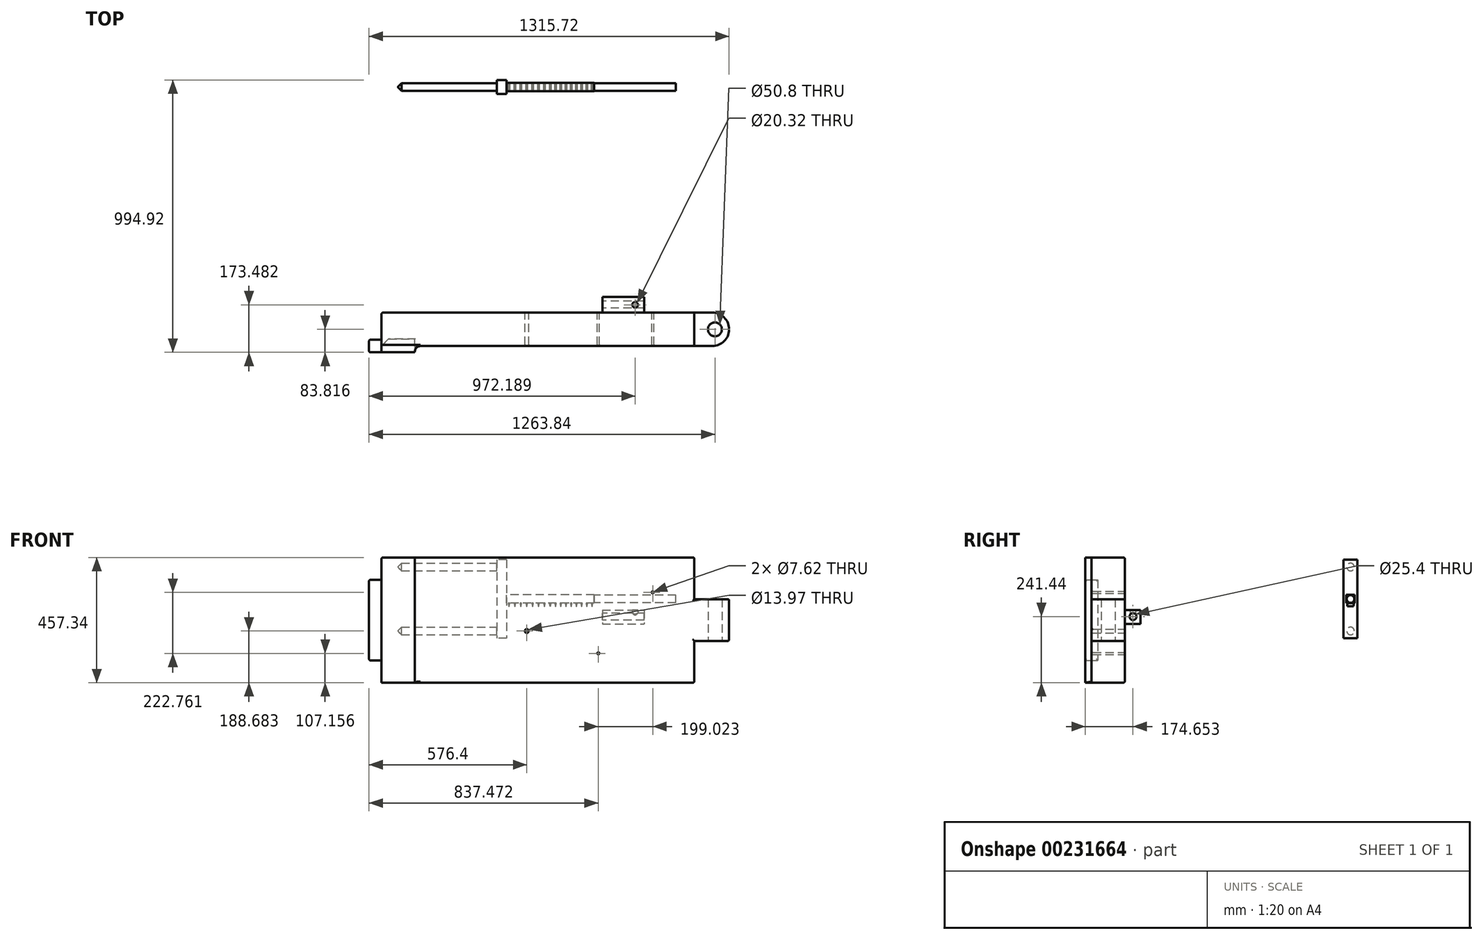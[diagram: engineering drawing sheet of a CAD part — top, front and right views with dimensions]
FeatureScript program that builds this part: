
annotation { "Feature Type Name" : "Feature", "Feature Type Description" : "" }
export const myFeature = defineFeature(function(context is Context, id is Id, definition is map)
    precondition{}
    {
        {
            var Q0;
            Q0=qCreatedBy(makeId("Right.planeOp"),FACE);
            var sketch = newSketch(context, id + "F0", { "sketchPlane" : qUnion([Q0])});
            skLineSegment(sketch, "E0", {"start": v(0, 0) * mm, "end": v(0, 121.92) * mm, "construction": true});
            skLineSegment(sketch, "E1", {"start": v(0, 0) * mm, "end": v(0, -121.92) * mm, "construction": true});
            skCircle(sketch, "E2", {"center": v(0, 121.92) * mm, "radius": 15.24 * mm});
            skCircle(sketch, "E3", {"center": v(0, -121.92) * mm, "radius": 15.24 * mm});
            skLineSegment(sketch, "E4.bottom", {"start": v(25.4, 143.51) * mm, "end": v(-25.4, 143.51) * mm});
            skLineSegment(sketch, "E4.top", {"start": v(25.4, -143.51) * mm, "end": v(-25.4, -143.51) * mm});
            skLineSegment(sketch, "E4.left", {"start": v(25.4, 143.51) * mm, "end": v(25.4, -143.51) * mm});
            skLineSegment(sketch, "E4.right", {"start": v(-25.4, 143.51) * mm, "end": v(-25.4, -143.51) * mm});
            skPoint(sketch, "E4.middle", {"position": v(0, 0) * mm});
            skLineSegment(sketch, "E5.bottom", {"start": v(15.24, -15.24) * mm, "end": v(-15.24, -15.24) * mm});
            skLineSegment(sketch, "E5.top", {"start": v(15.24, 15.24) * mm, "end": v(-15.24, 15.24) * mm});
            skLineSegment(sketch, "E5.left", {"start": v(15.24, -15.24) * mm, "end": v(15.24, 15.24) * mm});
            skLineSegment(sketch, "E5.right", {"start": v(-15.24, -15.24) * mm, "end": v(-15.24, 15.24) * mm});
            skSolve(sketch);
        }
        {
            var Q0;
            Q0 = qSketchRegion(id + "F0", true);
            var Q1;
            Q1=makeQuery(id+"F0.imprint","IMPRINT",FACE,{"disambiguationData":[TD([[makeQuery(id+"F0.imprint","IMPRINT",EDGE,{"derivedFrom":sQuery(id+"F0.wireOp",EDGE,"E2")}),1.0]])]});
            var Q2;
            Q2=makeQuery(id+"F0.imprint","IMPRINT",FACE,{"disambiguationData":[TD([[makeQuery(id+"F0.imprint","IMPRINT",EDGE,{"derivedFrom":sQuery(id+"F0.wireOp",EDGE,"E3")}),1.0]])]});
            extrude(context, id + "F1", {"entities" : qUnion([Q0, Q1, Q2]), "depth" : 35.56 * mm});
        }
        {
            var Q0;
            Q0=qCreatedBy(makeId("Right.planeOp"),FACE);
            var sketch = newSketch(context, id + "F2", { "sketchPlane" : qUnion([Q0])});
            skLineSegment(sketch, "E6.bottom", {"start": v(15.24, 15.24) * mm, "end": v(-15.24, 15.24) * mm});
            skLineSegment(sketch, "E6.top", {"start": v(15.24, -15.24) * mm, "end": v(-15.24, -15.24) * mm});
            skLineSegment(sketch, "E6.left", {"start": v(15.24, 15.24) * mm, "end": v(15.24, -15.24) * mm});
            skLineSegment(sketch, "E6.right", {"start": v(-15.24, 15.24) * mm, "end": v(-15.24, -15.24) * mm});
            skPoint(sketch, "E6.middle", {"position": v(0, 0) * mm});
            skSolve(sketch);
        }
        {
            var Q0;
            Q0=makeQuery(id+"F2.imprint","IMPRINT",FACE,{"disambiguationData":[TD([[makeQuery(id+"F2.imprint","IMPRINT",EDGE,{"derivedFrom":sQuery(id+"F2.wireOp",EDGE,"E6.bottom")}),1.0]])]});
            extrude(context, id + "F3", {"entities" : qUnion([Q0]), "operationType" : NewBodyOperationType.ADD, "depth" : 355.6 * mm});
        }
        {
            var Q0;
            Q0=qCreatedBy(makeId("Top.planeOp"),FACE);
            var sketch = newSketch(context, id + "F4", { "sketchPlane" : qUnion([Q0])});
            skLineSegment(sketch, "E7", {"start": v(35.48, 0) * mm, "end": v(355.44, 0) * mm, "construction": true});
            skLineSegment(sketch, "E8.bottom", {"start": v(198.63, 12.7) * mm, "end": v(192.28, 12.7) * mm});
            skLineSegment(sketch, "E8.top", {"start": v(198.63, -12.7) * mm, "end": v(192.28, -12.7) * mm});
            skLineSegment(sketch, "E8.left", {"start": v(198.63, 12.7) * mm, "end": v(198.63, -12.7) * mm});
            skLineSegment(sketch, "E8.right", {"start": v(192.28, 12.7) * mm, "end": v(192.28, -12.7) * mm});
            skPoint(sketch, "E8.middle", {"position": v(195.46, 0) * mm});
            skLineSegment(sketch, "E9.1.0.0", {"start": v(217.68, 12.7) * mm, "end": v(217.68, -12.7) * mm});
            skLineSegment(sketch, "E9.1.0.1", {"start": v(211.33, 12.7) * mm, "end": v(211.33, -12.7) * mm});
            skLineSegment(sketch, "E9.1.0.2", {"start": v(217.68, -12.7) * mm, "end": v(211.33, -12.7) * mm});
            skLineSegment(sketch, "E9.1.0.3", {"start": v(217.68, 12.7) * mm, "end": v(211.33, 12.7) * mm});
            skLineSegment(sketch, "E9.2.0.0", {"start": v(236.73, 12.7) * mm, "end": v(236.73, -12.7) * mm});
            skLineSegment(sketch, "E9.2.0.1", {"start": v(230.38, 12.7) * mm, "end": v(230.38, -12.7) * mm});
            skLineSegment(sketch, "E9.2.0.2", {"start": v(236.73, -12.7) * mm, "end": v(230.38, -12.7) * mm});
            skLineSegment(sketch, "E9.2.0.3", {"start": v(236.73, 12.7) * mm, "end": v(230.38, 12.7) * mm});
            skLineSegment(sketch, "E9.3.0.0", {"start": v(255.78, 12.7) * mm, "end": v(255.78, -12.7) * mm});
            skLineSegment(sketch, "E9.3.0.1", {"start": v(249.43, 12.7) * mm, "end": v(249.43, -12.7) * mm});
            skLineSegment(sketch, "E9.3.0.2", {"start": v(255.78, -12.7) * mm, "end": v(249.43, -12.7) * mm});
            skLineSegment(sketch, "E9.3.0.3", {"start": v(255.78, 12.7) * mm, "end": v(249.43, 12.7) * mm});
            skLineSegment(sketch, "E9.4.0.0", {"start": v(274.83, 12.7) * mm, "end": v(274.83, -12.7) * mm});
            skLineSegment(sketch, "E9.4.0.1", {"start": v(268.48, 12.7) * mm, "end": v(268.48, -12.7) * mm});
            skLineSegment(sketch, "E9.4.0.2", {"start": v(274.83, -12.7) * mm, "end": v(268.48, -12.7) * mm});
            skLineSegment(sketch, "E9.4.0.3", {"start": v(274.83, 12.7) * mm, "end": v(268.48, 12.7) * mm});
            skLineSegment(sketch, "E9.5.0.0", {"start": v(293.88, 12.7) * mm, "end": v(293.88, -12.7) * mm});
            skLineSegment(sketch, "E9.5.0.1", {"start": v(287.53, 12.7) * mm, "end": v(287.53, -12.7) * mm});
            skLineSegment(sketch, "E9.5.0.2", {"start": v(293.88, -12.7) * mm, "end": v(287.53, -12.7) * mm});
            skLineSegment(sketch, "E9.5.0.3", {"start": v(293.88, 12.7) * mm, "end": v(287.53, 12.7) * mm});
            skLineSegment(sketch, "E9.6.0.0", {"start": v(312.93, 12.7) * mm, "end": v(312.93, -12.7) * mm});
            skLineSegment(sketch, "E9.6.0.1", {"start": v(306.58, 12.7) * mm, "end": v(306.58, -12.7) * mm});
            skLineSegment(sketch, "E9.6.0.2", {"start": v(312.93, -12.7) * mm, "end": v(306.58, -12.7) * mm});
            skLineSegment(sketch, "E9.6.0.3", {"start": v(312.93, 12.7) * mm, "end": v(306.58, 12.7) * mm});
            skLineSegment(sketch, "E9.7.0.0", {"start": v(331.98, 12.7) * mm, "end": v(331.98, -12.7) * mm});
            skLineSegment(sketch, "E9.7.0.1", {"start": v(325.63, 12.7) * mm, "end": v(325.63, -12.7) * mm});
            skLineSegment(sketch, "E9.7.0.2", {"start": v(331.98, -12.7) * mm, "end": v(325.63, -12.7) * mm});
            skLineSegment(sketch, "E9.7.0.3", {"start": v(331.98, 12.7) * mm, "end": v(325.63, 12.7) * mm});
            skLineSegment(sketch, "E9.8.0.0", {"start": v(351.03, 12.7) * mm, "end": v(351.03, -12.7) * mm});
            skLineSegment(sketch, "E9.8.0.1", {"start": v(344.68, 12.7) * mm, "end": v(344.68, -12.7) * mm});
            skLineSegment(sketch, "E9.8.0.2", {"start": v(351.03, -12.7) * mm, "end": v(344.68, -12.7) * mm});
            skLineSegment(sketch, "E9.8.0.3", {"start": v(351.03, 12.7) * mm, "end": v(344.68, 12.7) * mm});
            skLineSegment(sketch, "E9.direction1", {"start": v(198.63, -12.7) * mm, "end": v(217.68, -12.7) * mm, "construction": true});
            skLineSegment(sketch, "E10.1.0.0", {"start": v(177.04, -12.7) * mm, "end": v(170.7, -12.7) * mm});
            skLineSegment(sketch, "E10.1.0.1", {"start": v(170.7, 12.7) * mm, "end": v(170.7, -12.7) * mm});
            skLineSegment(sketch, "E10.1.0.2", {"start": v(177.04, 12.7) * mm, "end": v(177.04, -12.7) * mm});
            skLineSegment(sketch, "E10.1.0.3", {"start": v(177.04, 12.7) * mm, "end": v(170.7, 12.7) * mm});
            skLineSegment(sketch, "E10.2.0.0", {"start": v(155.45, -12.7) * mm, "end": v(149.1, -12.7) * mm});
            skLineSegment(sketch, "E10.2.0.1", {"start": v(149.1, 12.7) * mm, "end": v(149.1, -12.7) * mm});
            skLineSegment(sketch, "E10.2.0.2", {"start": v(155.45, 12.7) * mm, "end": v(155.45, -12.7) * mm});
            skLineSegment(sketch, "E10.2.0.3", {"start": v(155.45, 12.7) * mm, "end": v(149.1, 12.7) * mm});
            skLineSegment(sketch, "E10.3.0.0", {"start": v(133.86, -12.7) * mm, "end": v(127.51, -12.7) * mm});
            skLineSegment(sketch, "E10.3.0.1", {"start": v(127.51, 12.7) * mm, "end": v(127.51, -12.7) * mm});
            skLineSegment(sketch, "E10.3.0.2", {"start": v(133.86, 12.7) * mm, "end": v(133.86, -12.7) * mm});
            skLineSegment(sketch, "E10.3.0.3", {"start": v(133.86, 12.7) * mm, "end": v(127.51, 12.7) * mm});
            skLineSegment(sketch, "E10.4.0.0", {"start": v(112.27, -12.7) * mm, "end": v(105.92, -12.7) * mm});
            skLineSegment(sketch, "E10.4.0.1", {"start": v(105.92, 12.7) * mm, "end": v(105.92, -12.7) * mm});
            skLineSegment(sketch, "E10.4.0.2", {"start": v(112.27, 12.7) * mm, "end": v(112.27, -12.7) * mm});
            skLineSegment(sketch, "E10.4.0.3", {"start": v(112.27, 12.7) * mm, "end": v(105.92, 12.7) * mm});
            skLineSegment(sketch, "E10.5.0.0", {"start": v(90.68, -12.7) * mm, "end": v(84.33, -12.7) * mm});
            skLineSegment(sketch, "E10.5.0.1", {"start": v(84.33, 12.7) * mm, "end": v(84.33, -12.7) * mm});
            skLineSegment(sketch, "E10.5.0.2", {"start": v(90.68, 12.7) * mm, "end": v(90.68, -12.7) * mm});
            skLineSegment(sketch, "E10.5.0.3", {"start": v(90.68, 12.7) * mm, "end": v(84.33, 12.7) * mm});
            skLineSegment(sketch, "E10.6.0.0", {"start": v(69.1, -12.7) * mm, "end": v(62.74, -12.7) * mm});
            skLineSegment(sketch, "E10.6.0.1", {"start": v(62.74, 12.7) * mm, "end": v(62.74, -12.7) * mm});
            skLineSegment(sketch, "E10.6.0.2", {"start": v(69.1, 12.7) * mm, "end": v(69.1, -12.7) * mm});
            skLineSegment(sketch, "E10.6.0.3", {"start": v(69.1, 12.7) * mm, "end": v(62.74, 12.7) * mm});
            skLineSegment(sketch, "E10.7.0.0", {"start": v(47.5, -12.7) * mm, "end": v(41.15, -12.7) * mm});
            skLineSegment(sketch, "E10.7.0.1", {"start": v(41.15, 12.7) * mm, "end": v(41.15, -12.7) * mm});
            skLineSegment(sketch, "E10.7.0.2", {"start": v(47.5, 12.7) * mm, "end": v(47.5, -12.7) * mm});
            skLineSegment(sketch, "E10.7.0.3", {"start": v(47.5, 12.7) * mm, "end": v(41.15, 12.7) * mm});
            skLineSegment(sketch, "E10.direction1", {"start": v(192.28, -12.7) * mm, "end": v(170.7, -12.7) * mm, "construction": true});
            skSolve(sketch);
        }
        {
            var Q0;
            Q0 = qSketchRegion(id + "F4", true);
            extrude(context, id + "F5", {"entities" : qUnion([Q0]), "operationType" : NewBodyOperationType.ADD, "oppositeDirection" : true, "depth" : 25.9 * mm, "hasDraft" : true, "draftAngle" : 3 * degree, "draftPullDirection" : true});
        }
        {
            var Q0;
            Q0=makeQuery(id+"F1.opExtrude","SWEPT_BODY",BODY,{"disambiguationData":[OSD([sQuery(id+"F0.wireOp",EDGE,"E4.bottom"),sQuery(id+"F0.wireOp",EDGE,"E4.top"),sQuery(id+"F0.wireOp",EDGE,"E4.left"),sQuery(id+"F0.wireOp",EDGE,"E4.right"),sQuery(id+"F0.wireOp",EDGE,"E5.bottom"),sQuery(id+"F0.wireOp",EDGE,"E5.top"),sQuery(id+"F0.wireOp",EDGE,"E5.left"),sQuery(id+"F0.wireOp",EDGE,"E5.right")])]});
            transform(context, id + "F6", {"entities" : qUnion([Q0]), "transformType" : TransformType.TRANSLATION_3D, "dx" : -19.05 * mm, "dy" : 0 * mm, "dz" : 0 * mm, "makeCopy" : false});
        }
        {
            var Q0;
            Q0=qCreatedBy(makeId("Right.planeOp"),FACE);
            var sketch = newSketch(context, id + "F7", { "sketchPlane" : qUnion([Q0])});
            skCircle(sketch, "E11", {"center": v(0, 116.84) * mm, "radius": 13.97 * mm});
            skCircle(sketch, "E12.MirrorC", {"center": v(0, -116.84) * mm, "radius": 13.97 * mm});
            skSolve(sketch);
        }
        {
            var Q0;
            Q0 = qSketchRegion(id + "F7", true);
            extrude(context, id + "F8", {"entities" : qUnion([Q0]), "operationType" : NewBodyOperationType.ADD, "oppositeDirection" : true, "depth" : 381 * mm});
        }
        {
            var Q0;
            Q0=makeQuery(id+"F1.opExtrude","SWEPT_BODY",BODY,{"disambiguationData":[OSD([sQuery(id+"F0.wireOp",EDGE,"E4.bottom"),sQuery(id+"F0.wireOp",EDGE,"E4.top"),sQuery(id+"F0.wireOp",EDGE,"E4.left"),sQuery(id+"F0.wireOp",EDGE,"E4.right"),sQuery(id+"F0.wireOp",EDGE,"E5.bottom"),sQuery(id+"F0.wireOp",EDGE,"E5.top"),sQuery(id+"F0.wireOp",EDGE,"E5.left"),sQuery(id+"F0.wireOp",EDGE,"E5.right")])]});
            transform(context, id + "F9", {"entities" : qUnion([Q0]), "transformType" : TransformType.TRANSLATION_3D, "dx" : 0 * mm, "dy" : 76.2 * mm, "dz" : 0 * mm, "makeCopy" : false});
        }
        {
            var Q0;
            Q0=qCreatedBy(makeId("Right.planeOp"),FACE);
            var sketch = newSketch(context, id + "F10", { "sketchPlane" : qUnion([Q0])});
            skCircle(sketch, "E13", {"center": v(76.2, 0) * mm, "radius": 13.97 * mm});
            skSolve(sketch);
        }
        {
            var Q0;
            Q0 = qSketchRegion(id + "F10", true);
            extrude(context, id + "F11", {"entities" : qUnion([Q0]), "operationType" : NewBodyOperationType.ADD, "depth" : 635 * mm});
        }
        {
            var Q0;
            Q0=qCreatedBy(makeId("Front.planeOp"),FACE);
            var sketch = newSketch(context, id + "F12", { "sketchPlane" : qUnion([Q0])});
            skLineSegment(sketch, "E14.bottom", {"start": v(692.51, 215.9) * mm, "end": v(-450.49, 215.9) * mm});
            skLineSegment(sketch, "E14.top", {"start": v(692.51, -241.3) * mm, "end": v(-450.49, -241.3) * mm});
            skLineSegment(sketch, "E14.left", {"start": v(692.51, 215.9) * mm, "end": v(692.51, -241.3) * mm});
            skLineSegment(sketch, "E14.right", {"start": v(-450.49, 215.9) * mm, "end": v(-450.49, -241.3) * mm});
            skLineSegment(sketch, "E15", {"start": v(16.69, -14.66) * mm, "end": v(80.19, -14.66) * mm, "construction": true});
            skLineSegment(sketch, "E16", {"start": v(80.19, -14.66) * mm, "end": v(80.19, -52.76) * mm, "construction": true});
            skCircle(sketch, "E17", {"center": v(80.19, -52.76) * mm, "radius": 6.99 * mm});
            skPoint(sketch, "E18.middle", {"position": v(387.6, 0) * mm});
            skPoint(sketch, "E19.orphan", {"position": v(335.96, 43.8) * mm});
            skPoint(sketch, "E20.left.start.orphan", {"position": v(335.96, 14.38) * mm});
            skPoint(sketch, "E20.top.start.orphan", {"position": v(335.96, -15.05) * mm});
            skLineSegment(sketch, "E21.bottom", {"start": v(356.6, 23.65) * mm, "end": v(509, 23.65) * mm});
            skLineSegment(sketch, "E21.top", {"start": v(356.6, -27.15) * mm, "end": v(509, -27.15) * mm});
            skLineSegment(sketch, "E21.left", {"start": v(356.6, 23.65) * mm, "end": v(356.6, -27.15) * mm});
            skLineSegment(sketch, "E21.right", {"start": v(509, 23.65) * mm, "end": v(509, -27.15) * mm});
            skLineSegment(sketch, "E22.bottom", {"start": v(819.51, 63.5) * mm, "end": v(565.51, 63.5) * mm});
            skLineSegment(sketch, "E22.top", {"start": v(819.51, -88.9) * mm, "end": v(565.51, -88.9) * mm});
            skLineSegment(sketch, "E22.left", {"start": v(819.51, 63.5) * mm, "end": v(819.51, -88.9) * mm});
            skLineSegment(sketch, "E22.right", {"start": v(565.51, 63.5) * mm, "end": v(565.51, -88.9) * mm});
            skPoint(sketch, "E22.middle", {"position": v(692.51, -12.7) * mm});
            skCircle(sketch, "E23", {"center": v(540.29, 88.48) * mm, "radius": 3.81 * mm});
            skCircle(sketch, "E24", {"center": v(341.26, -134.28) * mm, "radius": 3.81 * mm});
            skLineSegment(sketch, "E25", {"start": v(509, 23.65) * mm, "end": v(-407.1, 23.65) * mm, "construction": true});
            skLineSegment(sketch, "E26", {"start": v(509, -27.15) * mm, "end": v(-405.08, -27.15) * mm, "construction": true});
            skPoint(sketch, "E27.right.end.orphan", {"position": v(-296.24, 91.54) * mm});
            skPoint(sketch, "E28.right.end.orphan", {"position": v(-296.24, -137.06) * mm});
            skSolve(sketch);
        }
        {
            var Q0;
            Q0=makeQuery(id+"F12.imprint","IMPRINT",FACE,{"disambiguationData":[TD([[makeQuery(id+"F12.imprint","IMPRINT",EDGE,{"derivedFrom":sQuery(id+"F12.wireOp",EDGE,"E14.bottom")}),1.0]])]});
            var Q1;
            {var subQ5=sQuery(id+"F12.wireOp",EDGE,"E22.left");Q1=makeQuery(id+"F12.imprint","IMPRINT",FACE,{"disambiguationData":[TD([[makeQuery(id+"F12.imprint","IMPRINT",EDGE,{"derivedFrom":subQ5}),-1.0]])]});}
            var Q2;
            {var subQ5=sQuery(id+"F12.wireOp",EDGE,"E22.right");Q2=makeQuery(id+"F12.imprint","IMPRINT",FACE,{"disambiguationData":[TD([[makeQuery(id+"F12.imprint","IMPRINT",EDGE,{"derivedFrom":subQ5}),1.0]])]});}
            extrude(context, id + "F13", {"entities" : qUnion([Q0, Q1, Q2]), "depth" : 121.92 * mm});
        }
        {
            var Q0;
            Q0=makeQuery(id+"F1.opExtrude","SWEPT_BODY",BODY,{"disambiguationData":[OSD([sQuery(id+"F0.wireOp",EDGE,"E4.bottom"),sQuery(id+"F0.wireOp",EDGE,"E4.top"),sQuery(id+"F0.wireOp",EDGE,"E4.left"),sQuery(id+"F0.wireOp",EDGE,"E4.right"),sQuery(id+"F0.wireOp",EDGE,"E5.bottom"),sQuery(id+"F0.wireOp",EDGE,"E5.top"),sQuery(id+"F0.wireOp",EDGE,"E5.left"),sQuery(id+"F0.wireOp",EDGE,"E5.right")])]});
            transform(context, id + "F14", {"entities" : qUnion([Q0]), "transformType" : TransformType.TRANSLATION_3D, "dx" : 0 * mm, "dy" : 195.58 * mm, "dz" : 0 * mm, "makeCopy" : false});
        }
        {
            var Q0;
            Q0=makeQuery(id+"F1.opExtrude","SWEPT_BODY",BODY,{"disambiguationData":[OSD([sQuery(id+"F0.wireOp",EDGE,"E4.bottom"),sQuery(id+"F0.wireOp",EDGE,"E4.top"),sQuery(id+"F0.wireOp",EDGE,"E4.left"),sQuery(id+"F0.wireOp",EDGE,"E4.right"),sQuery(id+"F0.wireOp",EDGE,"E5.bottom"),sQuery(id+"F0.wireOp",EDGE,"E5.top"),sQuery(id+"F0.wireOp",EDGE,"E5.left"),sQuery(id+"F0.wireOp",EDGE,"E5.right")])]});
            transform(context, id + "F15", {"entities" : qUnion([Q0]), "transformType" : TransformType.TRANSLATION_3D, "dx" : 0 * mm, "dy" : 0 * mm, "dz" : 7.62 * mm, "makeCopy" : false});
        }
        {
            var Q0;
            Q0=makeQuery(id+"F12.imprint","IMPRINT",FACE,{"disambiguationData":[TD([[makeQuery(id+"F12.imprint","IMPRINT",EDGE,{"derivedFrom":sQuery(id+"F12.wireOp",EDGE,"E21.bottom")}),-1.0]])]});
            extrude(context, id + "F16", {"entities" : qUnion([Q0]), "operationType" : NewBodyOperationType.ADD, "depth" : 121.92 * mm, "hasSecondDirection" : true, "secondDirectionOppositeDirection" : true, "secondDirectionDepth" : 57.4 * mm});
        }
        {
            var Q0;
            Q0=makeQuery(id+"F1.opExtrude","SWEPT_BODY",BODY,{"disambiguationData":[OSD([sQuery(id+"F0.wireOp",EDGE,"E4.bottom"),sQuery(id+"F0.wireOp",EDGE,"E4.top"),sQuery(id+"F0.wireOp",EDGE,"E4.left"),sQuery(id+"F0.wireOp",EDGE,"E4.right"),sQuery(id+"F0.wireOp",EDGE,"E5.bottom"),sQuery(id+"F0.wireOp",EDGE,"E5.top"),sQuery(id+"F0.wireOp",EDGE,"E5.left"),sQuery(id+"F0.wireOp",EDGE,"E5.right")])]});
            transform(context, id + "F17", {"entities" : qUnion([Q0]), "transformType" : TransformType.TRANSLATION_3D, "dx" : 0 * mm, "dy" : -244.6 * mm, "dz" : 56.64 * mm, "makeCopy" : false});
        }
        {
            var Q0;
            Q0=qCreatedBy(makeId("Right.planeOp"),FACE);
            cPlane(context, id + "F18", {"entities" : qUnion([Q0]), "cplaneType" : CPlaneType.OFFSET, "offset" : 355.6 * mm, "width" : 152.4 * mm, "height" : 152.4 * mm});
        }
        {
            var Q0;
            Q0=qCreatedBy(id+"F18.planeOp",FACE);
            var sketch = newSketch(context, id + "F19", { "sketchPlane" : qUnion([Q0])});
            skCircle(sketch, "E29", {"center": v(29.87, 0) * mm, "radius": 12.7 * mm});
            skSolve(sketch);
        }
        {
            var Q0;
            Q0=sQuery(id+"F19.wireOp",VERTEX,"E29.center");
            var Q1;
            Q1=makeQuery(id+"F13.opExtrude","SWEPT_BODY",BODY,{"disambiguationData":[OSD([sQuery(id+"F12.wireOp",EDGE,"E14.bottom"),sQuery(id+"F12.wireOp",EDGE,"E14.top"),sQuery(id+"F12.wireOp",EDGE,"E14.left"),sQuery(id+"F12.wireOp",EDGE,"E14.right"),sQuery(id+"F12.wireOp",EDGE,"E17"),sQuery(id+"F12.wireOp",EDGE,"E21.bottom"),sQuery(id+"F12.wireOp",EDGE,"E21.top"),sQuery(id+"F12.wireOp",EDGE,"E21.left"),sQuery(id+"F12.wireOp",EDGE,"E21.right")])]});
            hole(context, id + "F20", {"style" : HoleStyle.C_SINK, "endStyle" : HoleEndStyle.THROUGH, "oppositeDirection" : true, "holeDiameter" : 25.4 * mm, "cSinkDiameter" : 25.4 * mm, "cSinkAngle" : 90 * degree, "locations" : qUnion([Q0]), "scope" : qUnion([Q1]), "isTappedThrough" : true});
        }
        {
            var Q0;
            Q0=makeQuery(id+"F13.opExtrude","CAP_EDGE",EDGE,{"disambiguationData":[OSD([sQuery(id+"F12.wireOp",EDGE,"E22.left")])],"isStart":true});
            var Q1;
            Q1=makeQuery(id+"F13.opExtrude","CAP_EDGE",EDGE,{"disambiguationData":[OSD([sQuery(id+"F12.wireOp",EDGE,"E22.left")])],"isStart":false});
            fillet(context, id + "F21", {"entities" : qUnion([Q0, Q1]), "radius" : 60.96 * mm, "tangentPropagation" : true, "allowEdgeOverflow" : false});
        }
        {
            var Q0;
            Q0=makeQuery(id+"F13.opExtrude","SWEPT_FACE",FACE,{"disambiguationData":[OSD([sQuery(id+"F12.wireOp",EDGE,"E22.top")])]});
            cPlane(context, id + "F22", {"entities" : qUnion([Q0]), "cplaneType" : CPlaneType.OFFSET, "offset" : 25.4 * mm, "width" : 152.4 * mm, "height" : 152.4 * mm});
        }
        {
            var Q0;
            Q0=qCreatedBy(id+"F22.planeOp",FACE);
            var sketch = newSketch(context, id + "F23", { "sketchPlane" : qUnion([Q0])});
            skLineSegment(sketch, "E30", {"start": v(832.57, -12.74) * mm, "end": v(680.2, -12.7) * mm, "construction": true});
            skLineSegment(sketch, "E31", {"start": v(680.2, -12.7) * mm, "end": v(832.6, 134.62) * mm, "construction": true});
            skLineSegment(sketch, "E32", {"start": v(832.6, 134.62) * mm, "end": v(832.57, -12.74) * mm, "construction": true});
            skLineSegment(sketch, "E33", {"start": v(832.57, -12.74) * mm, "end": v(680.2, 134.62) * mm, "construction": true});
            skPoint(sketch, "E34", {"position": v(767.63, 60.96) * mm});
            skPoint(sketch, "E34.positionSnap0", {"position": v(756.4, 60.96) * mm});
            skSolve(sketch);
        }
        {
            var Q0;
            Q0=sQuery(id+"F23.wireOp",VERTEX,"E34");
            var Q1;
            Q1=makeQuery(id+"F13.opExtrude","SWEPT_BODY",BODY,{"disambiguationData":[OSD([sQuery(id+"F12.wireOp",EDGE,"E14.bottom"),sQuery(id+"F12.wireOp",EDGE,"E14.top"),sQuery(id+"F12.wireOp",EDGE,"E14.left"),sQuery(id+"F12.wireOp",EDGE,"E14.right"),sQuery(id+"F12.wireOp",EDGE,"E17"),sQuery(id+"F12.wireOp",EDGE,"E21.bottom"),sQuery(id+"F12.wireOp",EDGE,"E21.top"),sQuery(id+"F12.wireOp",EDGE,"E21.left"),sQuery(id+"F12.wireOp",EDGE,"E21.right"),sQuery(id+"F12.wireOp",EDGE,"E22.bottom"),sQuery(id+"F12.wireOp",EDGE,"E22.top"),sQuery(id+"F12.wireOp",EDGE,"E22.left")])]});
            hole(context, id + "F24", {"style" : HoleStyle.SIMPLE, "endStyle" : HoleEndStyle.THROUGH, "holeDiameter" : 50.8 * mm, "locations" : qUnion([Q0]), "scope" : qUnion([Q1]), "isTappedThrough" : true});
        }
        {
            var Q0;
            Q0=makeQuery(id+"F13.opExtrude","CAP_EDGE",EDGE,{"disambiguationData":[OSD([sQuery(id+"F12.wireOp",EDGE,"E14.bottom")])],"isStart":true});
            var Q1;
            {var subQ0=sQuery(id+"F12.wireOp",EDGE,"E14.left");Q1=makeQuery(id+"F13.opExtrude","CAP_EDGE",EDGE,{"disambiguationData":[OSD([subQ0]),TDD([makeQuery(id+"F12.imprint","IMPRINT",EDGE,{"disambiguationData":[TD([[makeQuery(id+"F12.imprint","INTERSECT",VERTEX,{"derivedFrom":[sQuery(id+"F12.wireOp",EDGE,"E14.bottom"),subQ0]}),-1.0]])],"derivedFrom":subQ0})])],"isStart":true});}
            var Q2;
            {var subQ0=sQuery(id+"F12.wireOp",EDGE,"E14.left");Q2=makeQuery(id+"F13.opExtrude","CAP_EDGE",EDGE,{"disambiguationData":[OSD([subQ0]),TDD([makeQuery(id+"F12.imprint","IMPRINT",EDGE,{"disambiguationData":[TD([[makeQuery(id+"F12.imprint","INTERSECT",VERTEX,{"derivedFrom":[sQuery(id+"F12.wireOp",EDGE,"E14.top"),subQ0]}),1.0]])],"derivedFrom":subQ0})])],"isStart":true});}
            var Q3;
            Q3=makeQuery(id+"F13.opExtrude","CAP_EDGE",EDGE,{"disambiguationData":[OSD([sQuery(id+"F12.wireOp",EDGE,"E14.top")])],"isStart":true});
            var Q4;
            Q4=makeQuery(id+"F13.opExtrude","CAP_EDGE",EDGE,{"disambiguationData":[OSD([sQuery(id+"F12.wireOp",EDGE,"E14.right")])],"isStart":true});
            fillet(context, id + "F25", {"entities" : qUnion([Q0, Q1, Q2, Q3, Q4]), "radius" : 5.08 * mm, "tangentPropagation" : true, "allowEdgeOverflow" : false});
        }
        {
            var Q0;
            {var subQ0=sQuery(id+"F12.wireOp",EDGE,"E21.right");var subQ1=sQuery(id+"F12.wireOp",EDGE,"E21.left");var subQ2=sQuery(id+"F12.wireOp",EDGE,"E21.top");var subQ3=sQuery(id+"F12.wireOp",EDGE,"E21.bottom");Q0=makeQuery(id+"F16.boolean.opBoolean","MERGE",FACE,{"derivedFrom":[makeQuery(id+"F13.opExtrude","CAP_FACE",FACE,{"disambiguationData":[OSD([sQuery(id+"F12.wireOp",EDGE,"E14.bottom"),sQuery(id+"F12.wireOp",EDGE,"E14.top"),sQuery(id+"F12.wireOp",EDGE,"E14.left"),sQuery(id+"F12.wireOp",EDGE,"E14.right"),sQuery(id+"F12.wireOp",EDGE,"E17"),subQ3,subQ2,subQ1,subQ0,sQuery(id+"F12.wireOp",EDGE,"E22.bottom"),sQuery(id+"F12.wireOp",EDGE,"E22.top"),sQuery(id+"F12.wireOp",EDGE,"E22.left")])],"isStart":false}),makeQuery(id+"F16.opExtrude","CAP_FACE",FACE,{"disambiguationData":[OSD([subQ3,subQ2,subQ1,subQ0])],"isStart":false})]});}
            var Q1;
            Q1=makeQuery(id+"F13.opExtrude","SWEPT_FACE",FACE,{"disambiguationData":[OSD([sQuery(id+"F12.wireOp",EDGE,"E14.bottom")])]});
            var Q2;
            Q2=makeQuery(id+"F13.opExtrude","SWEPT_FACE",FACE,{"disambiguationData":[OSD([sQuery(id+"F12.wireOp",EDGE,"E14.top")])]});
            fillet(context, id + "F26", {"entities" : qUnion([Q0, Q1, Q2]), "radius" : 5.08 * mm, "tangentPropagation" : true, "allowEdgeOverflow" : false});
        }
        {
            var Q0;
            {var subQ0=sQuery(id+"F12.wireOp",EDGE,"E21.right");var subQ1=sQuery(id+"F12.wireOp",EDGE,"E21.left");var subQ2=sQuery(id+"F12.wireOp",EDGE,"E21.top");var subQ3=sQuery(id+"F12.wireOp",EDGE,"E21.bottom");Q0=makeQuery(id+"F16.boolean.opBoolean","MERGE",FACE,{"derivedFrom":[makeQuery(id+"F13.opExtrude","CAP_FACE",FACE,{"disambiguationData":[OSD([sQuery(id+"F12.wireOp",EDGE,"E14.bottom"),sQuery(id+"F12.wireOp",EDGE,"E14.top"),sQuery(id+"F12.wireOp",EDGE,"E14.left"),sQuery(id+"F12.wireOp",EDGE,"E14.right"),sQuery(id+"F12.wireOp",EDGE,"E17"),subQ3,subQ2,subQ1,subQ0,sQuery(id+"F12.wireOp",EDGE,"E22.bottom"),sQuery(id+"F12.wireOp",EDGE,"E22.top"),sQuery(id+"F12.wireOp",EDGE,"E22.left")])],"isStart":false}),makeQuery(id+"F16.opExtrude","CAP_FACE",FACE,{"disambiguationData":[OSD([subQ3,subQ2,subQ1,subQ0])],"isStart":false})]});}
            cPlane(context, id + "F27", {"entities" : qUnion([Q0]), "cplaneType" : CPlaneType.OFFSET, "offset" : 25.4 * mm, "oppositeDirection" : true, "width" : 152.4 * mm, "height" : 152.4 * mm});
        }
        {
            var Q0;
            Q0=qCreatedBy(id+"F27.planeOp",FACE);
            var sketch = newSketch(context, id + "F28", { "sketchPlane" : qUnion([Q0])});
            skLineSegment(sketch, "E35.bottom", {"start": v(-450.56, 215.76) * mm, "end": v(-328.64, 215.76) * mm});
            skLineSegment(sketch, "E35.top", {"start": v(-450.56, -241.44) * mm, "end": v(-328.64, -241.44) * mm});
            skLineSegment(sketch, "E35.left", {"start": v(-450.56, 215.76) * mm, "end": v(-450.56, -241.44) * mm});
            skLineSegment(sketch, "E35.right", {"start": v(-328.64, 215.76) * mm, "end": v(-328.64, -241.44) * mm});
            skSolve(sketch);
        }
        {
            var Q0;
            Q0 = qSketchRegion(id + "F28", true);
            extrude(context, id + "F29", {"entities" : qUnion([Q0]), "operationType" : NewBodyOperationType.ADD, "depth" : 48.26 * mm});
        }
        {
            var Q0;
            {var subQ0=sQuery(id+"F12.wireOp",EDGE,"E21.right");var subQ1=sQuery(id+"F12.wireOp",EDGE,"E21.left");var subQ2=sQuery(id+"F12.wireOp",EDGE,"E21.top");var subQ3=sQuery(id+"F12.wireOp",EDGE,"E21.bottom");Q0=makeQuery(id+"F29.boolean.opBoolean","INTERSECT",EDGE,{"derivedFrom":[makeQuery(id+"F16.boolean.opBoolean","MERGE",FACE,{"derivedFrom":[makeQuery(id+"F13.opExtrude","CAP_FACE",FACE,{"disambiguationData":[OSD([sQuery(id+"F12.wireOp",EDGE,"E14.bottom"),sQuery(id+"F12.wireOp",EDGE,"E14.top"),sQuery(id+"F12.wireOp",EDGE,"E14.left"),sQuery(id+"F12.wireOp",EDGE,"E14.right"),sQuery(id+"F12.wireOp",EDGE,"E17"),subQ3,subQ2,subQ1,subQ0,sQuery(id+"F12.wireOp",EDGE,"E22.bottom"),sQuery(id+"F12.wireOp",EDGE,"E22.top"),sQuery(id+"F12.wireOp",EDGE,"E22.left")])],"isStart":false}),makeQuery(id+"F16.opExtrude","CAP_FACE",FACE,{"disambiguationData":[OSD([subQ3,subQ2,subQ1,subQ0])],"isStart":false})]}),makeQuery(id+"F29.opExtrude","SWEPT_FACE",FACE,{"disambiguationData":[OSD([sQuery(id+"F28.wireOp",EDGE,"E35.right")])]})]});}
            fillet(context, id + "F30", {"entities" : qUnion([Q0]), "radius" : 20.32 * mm, "tangentPropagation" : true, "allowEdgeOverflow" : false});
        }
        {
            var Q0;
            Q0=makeQuery(id+"F13.opExtrude","SWEPT_BODY",BODY,{"disambiguationData":[OSD([sQuery(id+"F12.wireOp",EDGE,"E14.bottom"),sQuery(id+"F12.wireOp",EDGE,"E14.top"),sQuery(id+"F12.wireOp",EDGE,"E14.left"),sQuery(id+"F12.wireOp",EDGE,"E14.right"),sQuery(id+"F12.wireOp",EDGE,"E17"),sQuery(id+"F12.wireOp",EDGE,"E21.bottom"),sQuery(id+"F12.wireOp",EDGE,"E21.top"),sQuery(id+"F12.wireOp",EDGE,"E21.left"),sQuery(id+"F12.wireOp",EDGE,"E21.right"),sQuery(id+"F12.wireOp",EDGE,"E22.bottom"),sQuery(id+"F12.wireOp",EDGE,"E22.top"),sQuery(id+"F12.wireOp",EDGE,"E22.left")])]});
            transform(context, id + "F31", {"entities" : qUnion([Q0]), "transformType" : TransformType.TRANSLATION_3D, "dx" : 10.16 * mm, "dy" : 0 * mm, "dz" : 0 * mm, "makeCopy" : false});
        }
        {
            var Q0;
            Q0=makeQuery(id+"F29.opExtrude","CAP_EDGE",EDGE,{"disambiguationData":[OSD([sQuery(id+"F28.wireOp",EDGE,"E35.left")])],"isStart":true});
            chamfer(context, id + "F32", {"entities" : qUnion([Q0]), "width" : 25.4 * mm, "tangentPropagation" : true});
        }
        {
            var Q0;
            Q0=makeQuery(id+"F29.opExtrude","SWEPT_EDGE",EDGE,{"disambiguationData":[OSD([sQuery(id+"F28.wireOp",EDGE,"E35.bottom"),sQuery(id+"F28.wireOp",EDGE,"E35.left")])]});
            fillet(context, id + "F33", {"entities" : qUnion([Q0]), "radius" : 5.08 * mm, "tangentPropagation" : true, "allowEdgeOverflow" : false});
        }
        {
            var Q0;
            Q0=makeQuery(id+"F13.opExtrude","SWEPT_FACE",FACE,{"disambiguationData":[OSD([sQuery(id+"F12.wireOp",EDGE,"E14.right")])]});
            cPlane(context, id + "F34", {"entities" : qUnion([Q0]), "cplaneType" : CPlaneType.OFFSET, "offset" : 25.4 * mm, "oppositeDirection" : true, "width" : 152.4 * mm, "height" : 152.4 * mm});
        }
        {
            var Q0;
            Q0=qCreatedBy(id+"F34.planeOp",FACE);
            var sketch = newSketch(context, id + "F35", { "sketchPlane" : qUnion([Q0])});
            skLineSegment(sketch, "E36.bottom", {"start": v(144.75, 134.48) * mm, "end": v(99.03, 134.48) * mm});
            skLineSegment(sketch, "E36.top", {"start": v(144.75, -160.16) * mm, "end": v(99.03, -160.16) * mm});
            skLineSegment(sketch, "E36.left", {"start": v(144.75, 134.48) * mm, "end": v(144.75, -160.16) * mm});
            skLineSegment(sketch, "E36.right", {"start": v(99.03, 134.48) * mm, "end": v(99.03, -160.16) * mm});
            skSolve(sketch);
        }
        {
            var Q0;
            Q0 = qSketchRegion(id + "F35", true);
            extrude(context, id + "F36", {"entities" : qUnion([Q0]), "operationType" : NewBodyOperationType.ADD, "depth" : 71.12 * mm});
        }
        {
            var Q0;
            Q0=makeQuery(id+"F36.opExtrude","CAP_EDGE",EDGE,{"disambiguationData":[OSD([sQuery(id+"F35.wireOp",EDGE,"E36.right")])],"isStart":false});
            var Q1;
            Q1=makeQuery(id+"F36.opExtrude","CAP_EDGE",EDGE,{"disambiguationData":[OSD([sQuery(id+"F35.wireOp",EDGE,"E36.bottom")])],"isStart":false});
            var Q2;
            Q2=makeQuery(id+"F36.opExtrude","CAP_EDGE",EDGE,{"disambiguationData":[OSD([sQuery(id+"F35.wireOp",EDGE,"E36.left")])],"isStart":false});
            var Q3;
            Q3=makeQuery(id+"F36.opExtrude","CAP_EDGE",EDGE,{"disambiguationData":[OSD([sQuery(id+"F35.wireOp",EDGE,"E36.top")])],"isStart":false});
            fillet(context, id + "F37", {"entities" : qUnion([Q0, Q1, Q2, Q3]), "radius" : 5.08 * mm, "tangentPropagation" : true, "allowEdgeOverflow" : false});
        }
        {
            var Q0;
            Q0=makeQuery(id+"F16.opExtrude","SWEPT_FACE",FACE,{"disambiguationData":[OSD([sQuery(id+"F12.wireOp",EDGE,"E21.bottom")])]});
            cPlane(context, id + "F38", {"entities" : qUnion([Q0]), "cplaneType" : CPlaneType.OFFSET, "offset" : 22.86 * mm, "oppositeDirection" : true, "width" : 152.4 * mm, "height" : 152.4 * mm});
        }
        {
            var Q0;
            Q0=makeQuery(id+"F1.opExtrude","SWEPT_BODY",BODY,{"disambiguationData":[OSD([sQuery(id+"F0.wireOp",EDGE,"E4.bottom"),sQuery(id+"F0.wireOp",EDGE,"E4.top"),sQuery(id+"F0.wireOp",EDGE,"E4.left"),sQuery(id+"F0.wireOp",EDGE,"E4.right"),sQuery(id+"F0.wireOp",EDGE,"E5.bottom"),sQuery(id+"F0.wireOp",EDGE,"E5.top"),sQuery(id+"F0.wireOp",EDGE,"E5.left"),sQuery(id+"F0.wireOp",EDGE,"E5.right")])]});
            transform(context, id + "F39", {"entities" : qUnion([Q0]), "transformType" : TransformType.TRANSLATION_3D, "dx" : 0 * mm, "dy" : 797.56 * mm, "dz" : 0 * mm, "makeCopy" : false});
        }
        {
            var Q0;
            Q0=qCreatedBy(id+"F38.planeOp",FACE);
            var sketch = newSketch(context, id + "F40", { "sketchPlane" : qUnion([Q0])});
            skCircle(sketch, "E37", {"center": v(486.14, 28.7) * mm, "radius": 10.16 * mm});
            skSolve(sketch);
        }
        {
            var Q0;
            Q0=sQuery(id+"F40.wireOp",VERTEX,"E37.center");
            var Q1;
            Q1=makeQuery(id+"F13.opExtrude","SWEPT_BODY",BODY,{"disambiguationData":[OSD([sQuery(id+"F12.wireOp",EDGE,"E14.bottom"),sQuery(id+"F12.wireOp",EDGE,"E14.top"),sQuery(id+"F12.wireOp",EDGE,"E14.left"),sQuery(id+"F12.wireOp",EDGE,"E14.right"),sQuery(id+"F12.wireOp",EDGE,"E17"),sQuery(id+"F12.wireOp",EDGE,"E21.bottom"),sQuery(id+"F12.wireOp",EDGE,"E21.top"),sQuery(id+"F12.wireOp",EDGE,"E21.left"),sQuery(id+"F12.wireOp",EDGE,"E21.right"),sQuery(id+"F12.wireOp",EDGE,"E22.bottom"),sQuery(id+"F12.wireOp",EDGE,"E22.top"),sQuery(id+"F12.wireOp",EDGE,"E22.left")])]});
            hole(context, id + "F41", {"style" : HoleStyle.SIMPLE, "endStyle" : HoleEndStyle.THROUGH, "oppositeDirection" : true, "holeDiameter" : 20.32 * mm, "locations" : qUnion([Q0]), "scope" : qUnion([Q1]), "isTappedThrough" : true});
        }
        {
            var Q0;
            Q0=makeQuery(id+"F8.opExtrude","CAP_EDGE",EDGE,{"disambiguationData":[OSD([sQuery(id+"F7.wireOp",EDGE,"E11")])],"isStart":false});
            var Q1;
            Q1=makeQuery(id+"F8.opExtrude","CAP_EDGE",EDGE,{"disambiguationData":[OSD([sQuery(id+"F7.wireOp",EDGE,"E12.MirrorC")])],"isStart":false});
            chamfer(context, id + "F42", {"entities" : qUnion([Q0, Q1]), "width" : 13.72 * mm, "tangentPropagation" : true});
        }
    });
